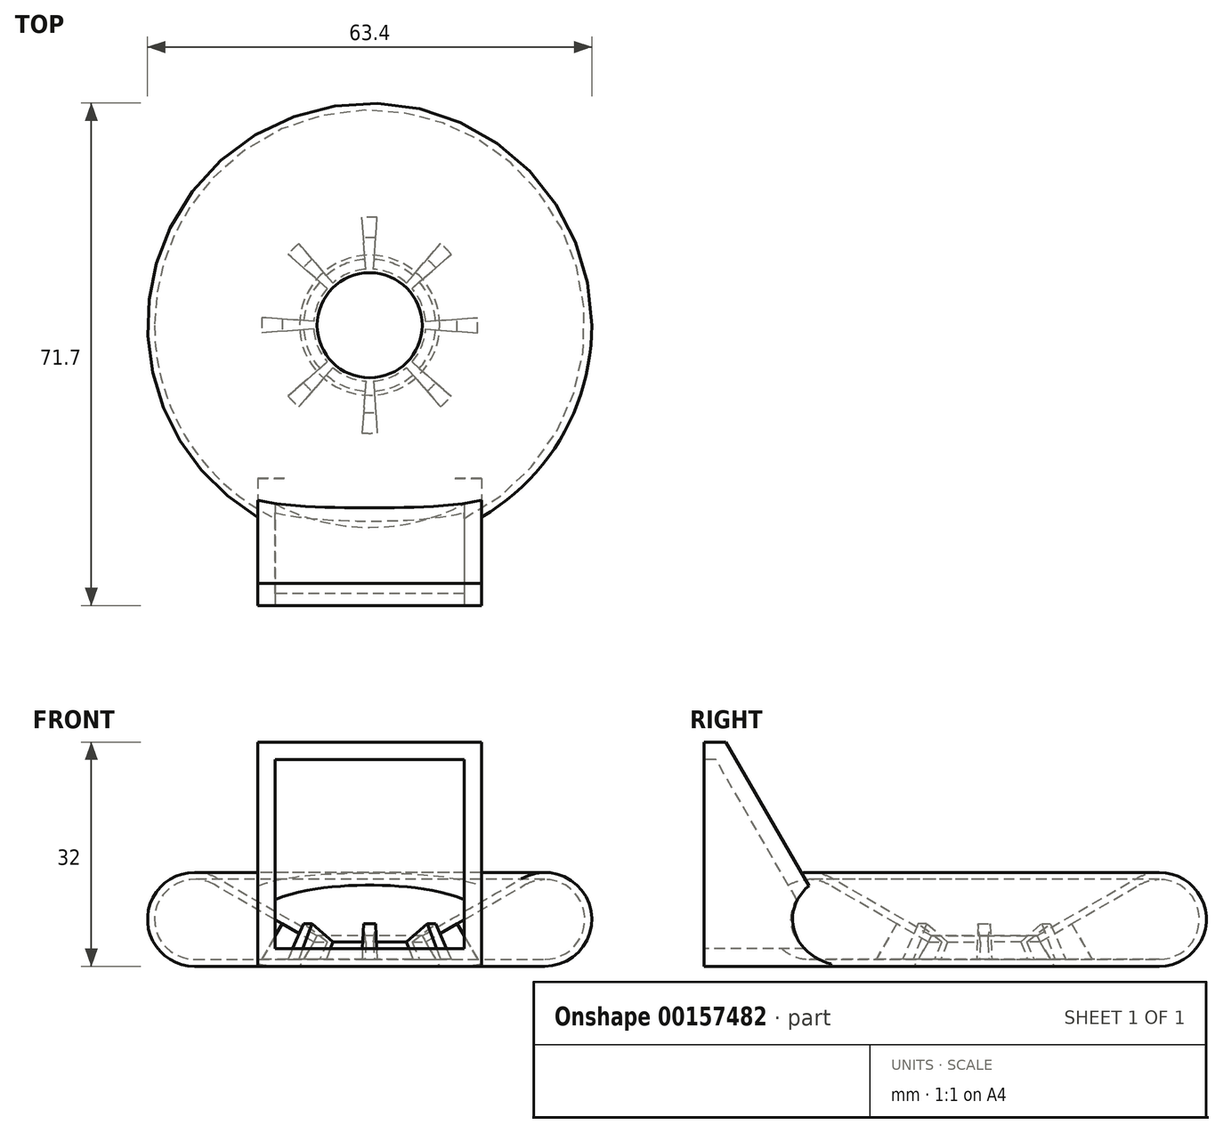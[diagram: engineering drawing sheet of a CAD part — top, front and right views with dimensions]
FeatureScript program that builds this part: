
annotation { "Feature Type Name" : "Feature", "Feature Type Description" : "" }
export const myFeature = defineFeature(function(context is Context, id is Id, definition is map)
    precondition{}
    {
        {
            var Q0;
            Q0=qCreatedBy(makeId("Front.planeOp"),FACE);
            var sketch = newSketch(context, id + "F0", { "sketchPlane" : qUnion([Q0])});
            skLineSegment(sketch, "E0", {"start": v(0, 47.4) * mm, "end": v(0, -26.39) * mm, "construction": true});
            skLineSegment(sketch, "E1", {"start": v(10, 0) * mm, "end": v(25, 0) * mm});
            skLineSegment(sketch, "E2", {"start": v(7.5, 4.33) * mm, "end": v(21.65, 12.5) * mm});
            skArc(sketch, "E3", {"start": v(25, 0) * mm, "mid": v(31.47, 8.43) * mm, "end": v(21.65, 12.5) * mm});
            skLineSegment(sketch, "E4", {"start": v(10, 0) * mm, "end": v(7.5, 4.33) * mm, "construction": true});
            skLineSegment(sketch, "E5", {"start": v(7.5, 4.33) * mm, "end": v(0, 0) * mm, "construction": true});
            skLineSegment(sketch, "E6.0", {"start": v(8, 3.46) * mm, "end": v(22.15, 11.63) * mm});
            skArc(sketch, "E6.1", {"start": v(25, 1) * mm, "mid": v(30.5, 8.17) * mm, "end": v(22.15, 11.63) * mm});
            skLineSegment(sketch, "E6.2", {"start": v(9.42, 1) * mm, "end": v(25, 1) * mm});
            skLineSegment(sketch, "E7", {"start": v(8, 3.46) * mm, "end": v(7.5, 4.33) * mm});
            skLineSegment(sketch, "E8", {"start": v(9.42, 1) * mm, "end": v(10, 0) * mm});
            skLineSegment(sketch, "E9", {"start": v(8, 3.46) * mm, "end": v(9.42, 1) * mm});
            skLineSegment(sketch, "E10", {"start": v(12.5, 6.06) * mm, "end": v(15.42, 1) * mm});
            skSolve(sketch);
        }
        {
            var Q0;
            Q0=makeQuery(id+"F0.imprint","IMPRINT",FACE,{"disambiguationData":[TD([[makeQuery(id+"F0.imprint","IMPRINT",EDGE,{"derivedFrom":sQuery(id+"F0.wireOp",EDGE,"E1")}),1.0]])]});
            var Q1;
            {var subQ0=sQuery(id+"F0.wireOp",EDGE,"E6.1");Q1=makeQuery(id+"F0.imprint","IMPRINT",FACE,{"disambiguationData":[TD([[makeQuery(id+"F0.imprint","IMPRINT",EDGE,{"derivedFrom":subQ0}),1.0]])]});}
            var Q2;
            {var subQ0=sQuery(id+"F0.wireOp",EDGE,"E9");Q2=makeQuery(id+"F0.imprint","IMPRINT",FACE,{"disambiguationData":[TD([[makeQuery(id+"F0.imprint","IMPRINT",EDGE,{"derivedFrom":subQ0}),1.0]])]});}
            var Q3;
            Q3=sQuery(id+"F0.wireOp",EDGE,"E0");
            revolve(context, id + "F1", {"entities" : qUnion([Q0, Q1, Q2]), "axis" : qUnion([Q3]), "revolveType" : RevolveType.FULL});
        }
        {
            var Q0;
            {var subQ0=sQuery(id+"F0.wireOp",EDGE,"E9");Q0=makeQuery(id+"F0.imprint","IMPRINT",FACE,{"disambiguationData":[TD([[makeQuery(id+"F0.imprint","IMPRINT",EDGE,{"derivedFrom":subQ0}),1.0]])]});}
            var sketch = newSketch(context, id + "F2", { "sketchPlane" : qUnion([Q0])});
            skSolve(sketch);
        }
        {
            var Q0;
            Q0=qCreatedBy(makeId("Front.planeOp"),FACE);
            cPlane(context, id + "F3", {"entities" : qUnion([Q0]), "cplaneType" : CPlaneType.OFFSET, "offset" : 40 * mm, "width" : 150 * mm, "height" : 150 * mm});
        }
        {
            var Q0;
            Q0=qCreatedBy(id+"F3.planeOp",FACE);
            var sketch = newSketch(context, id + "F4", { "sketchPlane" : qUnion([Q0])});
            skLineSegment(sketch, "E11.bottom", {"start": v(16, 32) * mm, "end": v(-16, 32) * mm});
            skLineSegment(sketch, "E11.top", {"start": v(16, 0) * mm, "end": v(-16, 0) * mm});
            skLineSegment(sketch, "E11.left", {"start": v(16, 32) * mm, "end": v(16, 0) * mm});
            skLineSegment(sketch, "E11.right", {"start": v(-16, 32) * mm, "end": v(-16, 0) * mm});
            skSolve(sketch);
        }
        {
            var Q0;
            Q0=makeQuery(id+"F4.imprint","IMPRINT",FACE,{"disambiguationData":[TD([[makeQuery(id+"F4.imprint","IMPRINT",EDGE,{"derivedFrom":sQuery(id+"F4.wireOp",EDGE,"E11.bottom")}),1.0]])]});
            var Q1;
            Q1=makeQuery(id+"F1.opRevolve","SWEPT_FACE",FACE,{"disambiguationData":[OSD([sQuery(id+"F0.wireOp",EDGE,"E3")])]});
            var Q2;
            Q2=makeQuery(id+"F1.opRevolve","SWEPT_BODY",BODY,{"disambiguationData":[OSD([sQuery(id+"F0.wireOp",EDGE,"E1"),sQuery(id+"F0.wireOp",EDGE,"E2"),sQuery(id+"F0.wireOp",EDGE,"E3"),sQuery(id+"F0.wireOp",EDGE,"E6.0"),sQuery(id+"F0.wireOp",EDGE,"E6.1"),sQuery(id+"F0.wireOp",EDGE,"E6.2"),sQuery(id+"F0.wireOp",EDGE,"E7"),sQuery(id+"F0.wireOp",EDGE,"E8")])]});
            extrude(context, id + "F5", {"entities" : qUnion([Q0]), "operationType" : NewBodyOperationType.ADD, "oppositeDirection" : true, "endBoundEntityFace" : qUnion([Q1]), "endBoundEntityBody" : qUnion([Q2]), "depth" : 18.15 * mm});
        }
        {
            var Q0;
            Q0=makeQuery(id+"F5.opExtrude","CAP_EDGE",EDGE,{"disambiguationData":[OSD([sQuery(id+"F4.wireOp",EDGE,"E11.bottom")])],"isStart":false});
            chamfer(context, id + "F6", {"entities" : qUnion([Q0]), "chamferType" : ChamferType.OFFSET_ANGLE, "width" : 15 * mm, "oppositeDirection" : false, "angle" : 60 * degree, "tangentPropagation" : true});
        }
        {
            var Q0;
            Q0=makeQuery(id+"F5.opExtrude","CAP_FACE",FACE,{"disambiguationData":[OSD([sQuery(id+"F4.wireOp",EDGE,"E11.bottom"),sQuery(id+"F4.wireOp",EDGE,"E11.top"),sQuery(id+"F4.wireOp",EDGE,"E11.left"),sQuery(id+"F4.wireOp",EDGE,"E11.right")])],"isStart":true});
            shell(context, id + "F7", {"entities" : qUnion([Q0]), "thickness" : 2.5 * mm});
        }
        {
            var Q0;
            {var subQ0=sQuery(id+"F0.wireOp",EDGE,"E6.1");Q0=makeQuery(id+"F0.imprint","IMPRINT",FACE,{"disambiguationData":[TD([[makeQuery(id+"F0.imprint","IMPRINT",EDGE,{"derivedFrom":subQ0}),1.0]])]});}
            var Q1;
            {var subQ0=sQuery(id+"F0.wireOp",EDGE,"E9");Q1=makeQuery(id+"F2.imprint","IMPRINT",FACE,{"disambiguationData":[TD([[makeQuery(id+"F2.imprint","IMPRINT",EDGE,{"derivedFrom":makeQuery(id+"F0.imprint","IMPRINT",EDGE,{"derivedFrom":subQ0})}),1.0]])]});}
            var Q2;
            Q2=sQuery(id+"F0.wireOp",EDGE,"E0");
            revolve(context, id + "F8", {"operationType" : NewBodyOperationType.REMOVE, "entities" : qUnion([Q0, Q1]), "axis" : qUnion([Q2]), "revolveType" : RevolveType.FULL, "oppositeDirection" : true});
        }
        {
            var Q0;
            {var subQ0=sQuery(id+"F0.wireOp",EDGE,"E9");Q0=makeQuery(id+"F0.imprint","IMPRINT",FACE,{"disambiguationData":[TD([[makeQuery(id+"F0.imprint","IMPRINT",EDGE,{"derivedFrom":subQ0}),1.0]])]});}
            var Q1;
            Q1=sQuery(id+"F0.wireOp",EDGE,"E0");
            revolve(context, id + "F9", {"entities" : qUnion([Q0]), "axis" : qUnion([Q1]), "revolveType" : RevolveType.SYMMETRIC, "angle" : 8 * degree});
        }
        {
            var Q0;
            Q0=makeQuery(id+"F9.opRevolve","SWEPT_BODY",BODY,{"disambiguationData":[OSD([sQuery(id+"F0.wireOp",EDGE,"E6.0"),sQuery(id+"F0.wireOp",EDGE,"E6.2"),sQuery(id+"F0.wireOp",EDGE,"E9"),sQuery(id+"F0.wireOp",EDGE,"E10")])]});
            var Q1;
            Q1=makeQuery(id+"F1.opRevolve","SWEPT_EDGE",EDGE,{"disambiguationData":[OSD([sQuery(id+"F0.wireOp",EDGE,"E2"),sQuery(id+"F0.wireOp",EDGE,"E7")])]});
            circularPattern(context, id + "F10", {"operationType" : NewBodyOperationType.ADD, "entities" : qUnion([Q0]), "axis" : qUnion([Q1]), "angle" : 360 * degree, "instanceCount" : 8, "equalSpace" : true});
        }
    });
